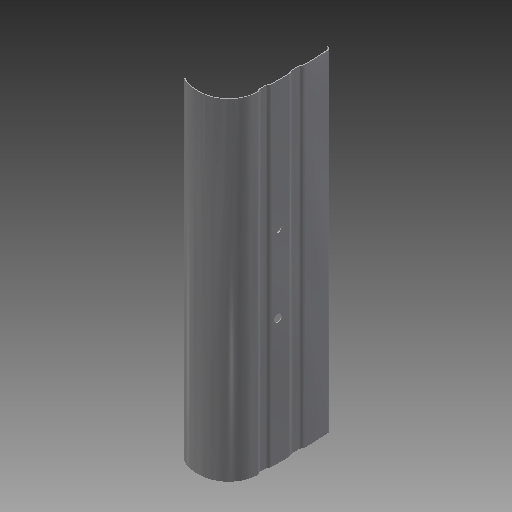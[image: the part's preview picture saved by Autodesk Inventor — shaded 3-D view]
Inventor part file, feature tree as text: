
AUTODESK INVENTOR PART (.ipt)
format: ipt  version: 2019 (Build 230136000, 136)  size: 256,000 bytes
history: native  units: mm
features: fillet x4, other x2, sketch x2, extrude x1, hole x1
ambient origin geometry x8: Origin, YZ Plane, XZ Plane, XY Plane, X Axis, Y Axis, Z Axis, Center Point
bodies: Solid1 (feature_tree)
feature tree (10):
  extrude  "Extrusion1"  Depth=11.611876mm
  fillet  "Fillet1"  Radius=0.748339mm
  fillet  "Fillet2"  Radius=31.438396mm
  fillet  "Fillet3"  Radius=32.205711mm
  fillet  "Fillet4"  Radius=61.949742mm
  hole  "Hole1"  [1 undecoded]
  other  "Work Axis1"
  other  "Work Axis2"
  sketch  "Sketch2"  dims[d0=86.75mm d1=11.611876mm d2=0.748339mm d3=31.438396mm d4=32.205711mm d5=61.949742mm]
  sketch  "Sketch3"  dims[d6=33.604449mm d7=4.0mm d8=5.759587mm d9=4.973861mm d10=18.517757mm d11=1.0mm d12=1.0mm d13=31.0mm d14=31.0mm d15=6.981317mm d16=10.0mm d17=3.0mm d18=1.0mm d19=1.0mm d20=1.0mm d21=40.0mm d22=11.0mm d23=1.0mm d24=1.0mm d25=1.0mm d26=28.51479mm d27=1.0mm d28=1.0mm d29=1.0mm d30=384.5mm d31=0.0mm d32=6.0mm d33=5.0mm d34=7.0mm d35=3.0mm d36=4.0mm d37=90.000015mm d38=23.137093mm d39=46.451296mm d40=9.0mm d41=6.0mm d42=4.0mm d43=2.0mm d44=90.0deg d45=8.0mm d46=20.594885mm]
note: 1 required parameter value undecoded (feature->parameter linkage not recoverable at this tier; creation-order binding heuristic only, values carry confidence <= 0.55)
